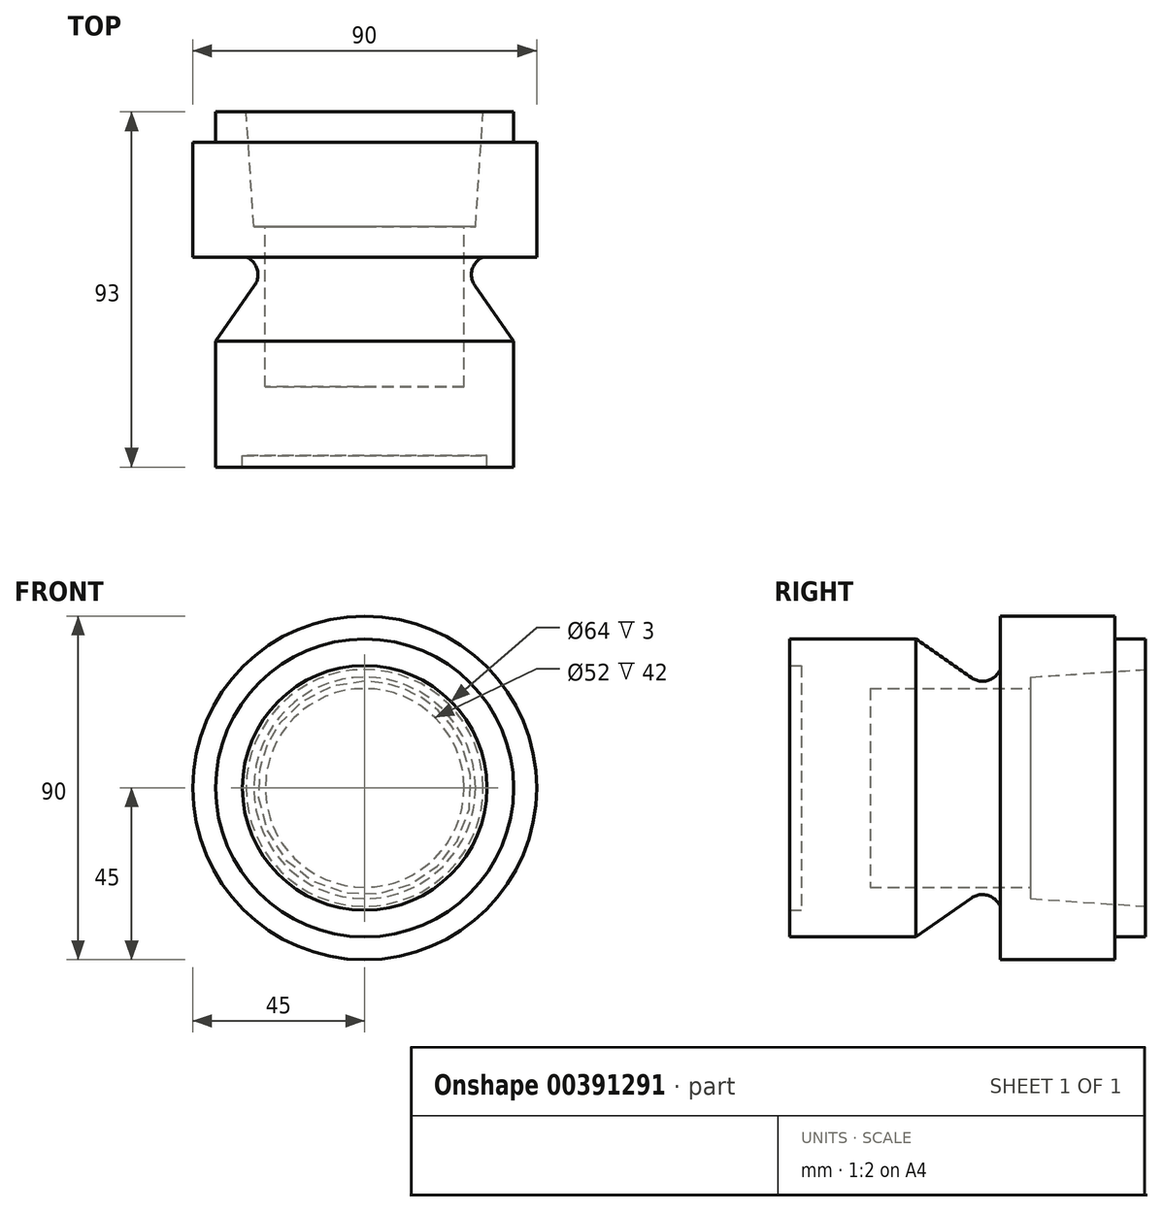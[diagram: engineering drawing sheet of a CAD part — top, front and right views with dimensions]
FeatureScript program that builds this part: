
annotation { "Feature Type Name" : "Feature", "Feature Type Description" : "" }
export const myFeature = defineFeature(function(context is Context, id is Id, definition is map)
    precondition{}
    {
        {
            var Q0;
            Q0=qCreatedBy(makeId("Right.planeOp"),FACE);
            var sketch = newSketch(context, id + "F0", { "sketchPlane" : qUnion([Q0])});
            skLineSegment(sketch, "E0", {"start": v(0, 13) * mm, "end": v(33, 13) * mm});
            skLineSegment(sketch, "E1", {"start": v(33, 13) * mm, "end": v(47.52, 2.83) * mm});
            skArc(sketch, "E2", {"start": v(47.52, 2.83) * mm, "mid": v(51.78, 2.13) * mm, "end": v(55, 5) * mm});
            skLineSegment(sketch, "E3", {"start": v(55, 5) * mm, "end": v(55, 19) * mm});
            skLineSegment(sketch, "E4", {"start": v(55, 19) * mm, "end": v(85, 19) * mm});
            skLineSegment(sketch, "E5", {"start": v(85, 19) * mm, "end": v(85, 13) * mm});
            skLineSegment(sketch, "E6", {"start": v(85, 13) * mm, "end": v(93, 13) * mm});
            skLineSegment(sketch, "E7", {"start": v(93, 13) * mm, "end": v(93, 5) * mm});
            skLineSegment(sketch, "E8", {"start": v(93, 5) * mm, "end": v(63, 3) * mm});
            skLineSegment(sketch, "E9", {"start": v(63, 3) * mm, "end": v(63, 0) * mm});
            skLineSegment(sketch, "E10", {"start": v(63, 0) * mm, "end": v(21, 0) * mm});
            skLineSegment(sketch, "E11", {"start": v(21, 0) * mm, "end": v(21, -26) * mm});
            skPoint(sketch, "E12.end.orphan", {"position": v(0, -26.1) * mm});
            skLineSegment(sketch, "E13", {"start": v(21, -26) * mm, "end": v(3, -26) * mm});
            skPoint(sketch, "E14.end.orphan", {"position": v(0, 0) * mm});
            skPoint(sketch, "E14.start.orphan", {"position": v(3, 0) * mm});
            skLineSegment(sketch, "E15", {"start": v(3, -26) * mm, "end": v(3, 6) * mm});
            skLineSegment(sketch, "E16", {"start": v(3, 6) * mm, "end": v(0, 6) * mm});
            skLineSegment(sketch, "E17", {"start": v(0, 6) * mm, "end": v(0, 13) * mm});
            skSolve(sketch);
        }
        {
            var Q0;
            Q0 = qSketchRegion(id + "F0", true);
            var Q1;
            Q1=sQuery(id+"F0.wireOp",EDGE,"E13");
            revolve(context, id + "F1", {"entities" : qUnion([Q0]), "axis" : qUnion([Q1]), "revolveType" : RevolveType.FULL});
        }
    });
